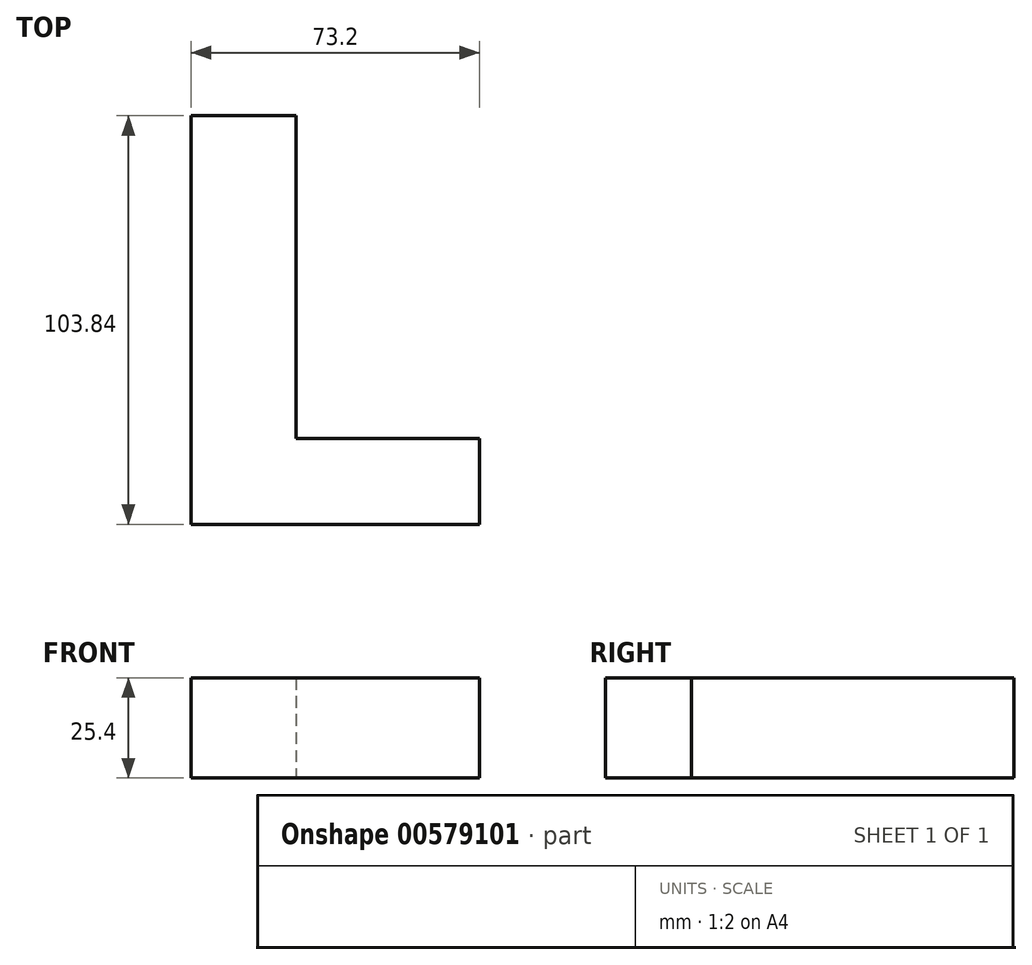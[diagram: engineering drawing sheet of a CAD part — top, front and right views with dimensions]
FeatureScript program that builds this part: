
annotation { "Feature Type Name" : "Feature", "Feature Type Description" : "" }
export const myFeature = defineFeature(function(context is Context, id is Id, definition is map)
    precondition{}
    {
        {
            var Q0;
            Q0=qCreatedBy(makeId("Top.planeOp"),FACE);
            var sketch = newSketch(context, id + "F0", { "sketchPlane" : qUnion([Q0])});
            skLineSegment(sketch, "E0", {"start": v(-56.74, 49.94) * mm, "end": v(-56.74, -48.8) * mm});
            skLineSegment(sketch, "E1", {"start": v(-56.74, -48.8) * mm, "end": v(16.46, -48.8) * mm});
            skLineSegment(sketch, "E2", {"start": v(16.46, -48.8) * mm, "end": v(16.46, -26.95) * mm});
            skLineSegment(sketch, "E3", {"start": v(16.46, -26.95) * mm, "end": v(-30.07, -26.95) * mm});
            skLineSegment(sketch, "E4", {"start": v(-30.07, -26.95) * mm, "end": v(-30.07, 55.04) * mm});
            skLineSegment(sketch, "E5", {"start": v(-29.8, 55.04) * mm, "end": v(-56.74, 55.04) * mm});
            skLineSegment(sketch, "E6", {"start": v(-56.74, 55.04) * mm, "end": v(-56.74, 49.94) * mm});
            skSolve(sketch);
        }
        {
            var Q0;
            Q0 = qSketchRegion(id + "F0", true);
            extrude(context, id + "F1", {"entities" : qUnion([Q0]), "depth" : 25.4 * mm, "offsetDistance" : 25.4 * mm});
        }
    });
